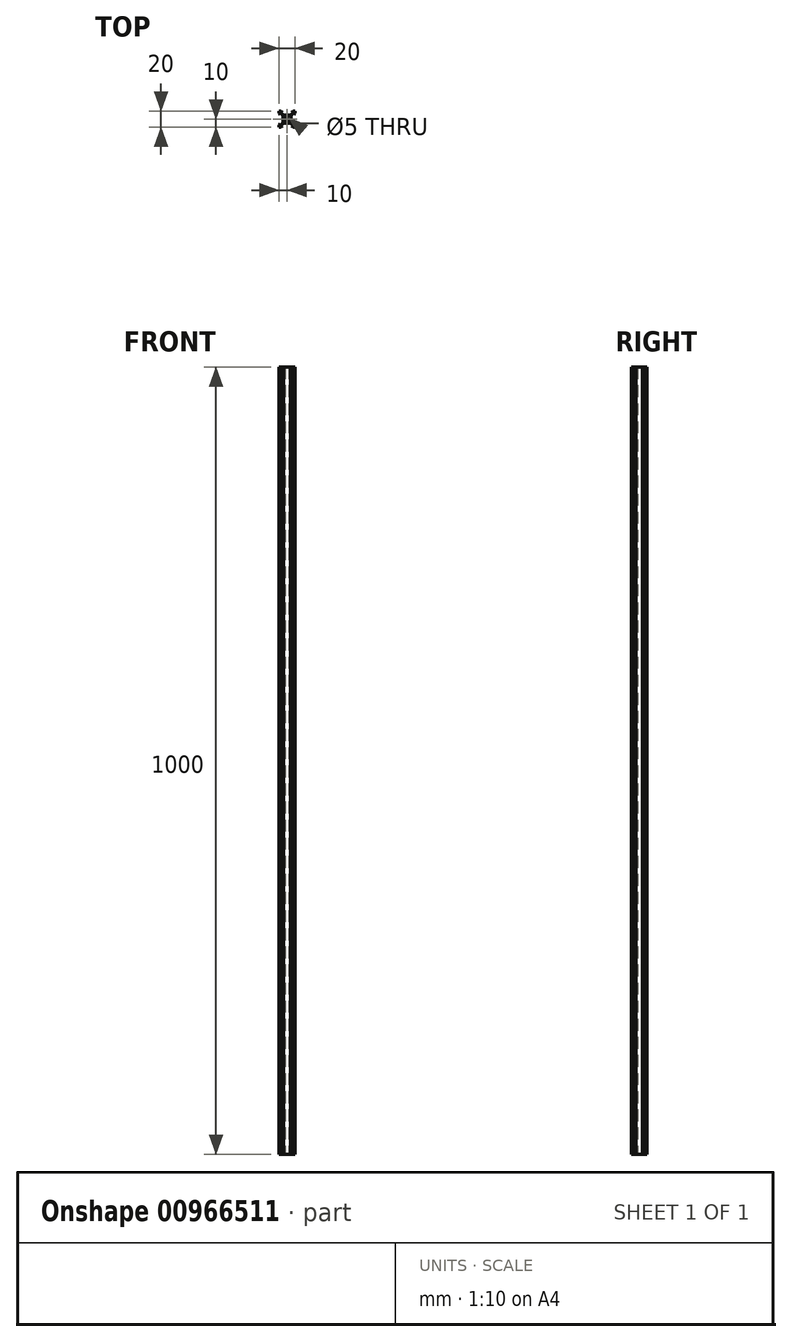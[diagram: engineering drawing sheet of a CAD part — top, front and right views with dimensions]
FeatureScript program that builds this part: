
annotation { "Feature Type Name" : "Feature", "Feature Type Description" : "" }
export const myFeature = defineFeature(function(context is Context, id is Id, definition is map)
    precondition{}
    {
        {
            var Q0;
            Q0=qCreatedBy(makeId("Top.planeOp"),FACE);
            var sketch = newSketch(context, id + "F0", { "sketchPlane" : qUnion([Q0])});
            skCircle(sketch, "E0", {"center": v(0, 0) * mm, "radius": 2.5 * mm});
            skLineSegment(sketch, "E1.bottom", {"start": v(4.25, 5) * mm, "end": v(-4.25, 5) * mm});
            skLineSegment(sketch, "E1.top", {"start": v(4.25, -5) * mm, "end": v(-4.25, -5) * mm});
            skLineSegment(sketch, "E1.left", {"start": v(5, 4.25) * mm, "end": v(5, -4.25) * mm});
            skLineSegment(sketch, "E1.right", {"start": v(-5, 4.25) * mm, "end": v(-5, -4.25) * mm});
            skLineSegment(sketch, "E2.bottom", {"start": v(10, 10) * mm, "end": v(7.5, 10) * mm});
            skLineSegment(sketch, "E2.top", {"start": v(10, -10) * mm, "end": v(7.5, -10) * mm});
            skLineSegment(sketch, "E2.left", {"start": v(10, 10) * mm, "end": v(10, 7.5) * mm});
            skLineSegment(sketch, "E2.right", {"start": v(-10, 10) * mm, "end": v(-10, 7.52) * mm});
            skLineSegment(sketch, "E3.bottom", {"start": v(7.5, 9) * mm, "end": v(5.88, 9) * mm});
            skLineSegment(sketch, "E3.top", {"start": v(7.5, -9) * mm, "end": v(5.87, -9) * mm});
            skLineSegment(sketch, "E3.left", {"start": v(7.5, 9) * mm, "end": v(7.5, 8.25) * mm});
            skLineSegment(sketch, "E3.right", {"start": v(-7.5, 9) * mm, "end": v(-7.5, 8.25) * mm});
            skLineSegment(sketch, "E4.bottom", {"start": v(9, 7.5) * mm, "end": v(8.25, 7.5) * mm});
            skLineSegment(sketch, "E4.top", {"start": v(9, -7.5) * mm, "end": v(8.25, -7.5) * mm});
            skLineSegment(sketch, "E4.left", {"start": v(9, 7.5) * mm, "end": v(9, 5.94) * mm});
            skLineSegment(sketch, "E4.right", {"start": v(-9, 7.5) * mm, "end": v(-9, 5.74) * mm});
            skLineSegment(sketch, "E5.trimOffspring", {"start": v(-8.25, 7.5) * mm, "end": v(-9, 7.5) * mm});
            skLineSegment(sketch, "E6.trimOffspring", {"start": v(-7.5, -8.25) * mm, "end": v(-7.5, -9) * mm});
            skLineSegment(sketch, "E7.trimOffspring", {"start": v(7.5, -8.25) * mm, "end": v(7.5, -9) * mm});
            skLineSegment(sketch, "E8.trimOffspring", {"start": v(-8.25, -7.5) * mm, "end": v(-9, -7.5) * mm});
            skLineSegment(sketch, "E9", {"start": v(-7.5, 8.25) * mm, "end": v(-4.25, 5) * mm});
            skLineSegment(sketch, "E10", {"start": v(-8.25, 7.5) * mm, "end": v(-5, 4.25) * mm});
            skLineSegment(sketch, "E11", {"start": v(8.25, -7.5) * mm, "end": v(5, -4.25) * mm});
            skLineSegment(sketch, "E12", {"start": v(7.5, -8.25) * mm, "end": v(4.25, -5) * mm});
            skLineSegment(sketch, "E13", {"start": v(-8.25, -7.5) * mm, "end": v(-5, -4.25) * mm});
            skLineSegment(sketch, "E14", {"start": v(-7.5, -8.25) * mm, "end": v(-4.25, -5) * mm});
            skLineSegment(sketch, "E15", {"start": v(7.5, 8.25) * mm, "end": v(4.25, 5) * mm});
            skLineSegment(sketch, "E16", {"start": v(8.25, 7.5) * mm, "end": v(5, 4.25) * mm});
            skPoint(sketch, "E17.orphan", {"position": v(-7.5, 7.5) * mm});
            skPoint(sketch, "E18.orphan", {"position": v(7.5, 7.5) * mm});
            skPoint(sketch, "E19.orphan", {"position": v(-7.5, -7.5) * mm});
            skPoint(sketch, "E20.orphan", {"position": v(7.5, -7.5) * mm});
            skPoint(sketch, "E21.orphan", {"position": v(-5, -5) * mm});
            skPoint(sketch, "E22.orphan", {"position": v(5, -5) * mm});
            skPoint(sketch, "E23.orphan", {"position": v(5, 5) * mm});
            skPoint(sketch, "E24.orphan", {"position": v(-5, 5) * mm});
            skLineSegment(sketch, "E25", {"start": v(-7.5, 10) * mm, "end": v(-5.62, 9) * mm});
            skLineSegment(sketch, "E26", {"start": v(7.5, 10) * mm, "end": v(5.88, 9) * mm});
            skPoint(sketch, "E26.endSnap0", {"position": v(5.88, 6.63) * mm});
            skLineSegment(sketch, "E27", {"start": v(10, 7.5) * mm, "end": v(9, 5.94) * mm});
            skLineSegment(sketch, "E28", {"start": v(10, -7.5) * mm, "end": v(9, -5.87) * mm});
            skPoint(sketch, "E28.endSnap0", {"position": v(6.62, -5.87) * mm});
            skLineSegment(sketch, "E29", {"start": v(7.5, -10) * mm, "end": v(5.87, -9) * mm});
            skPoint(sketch, "E29.endSnap0", {"position": v(5.87, -6.62) * mm});
            skLineSegment(sketch, "E30", {"start": v(-7.5, -10) * mm, "end": v(-5.45, -9) * mm});
            skLineSegment(sketch, "E31", {"start": v(-10, -7.5) * mm, "end": v(-9, -5.54) * mm});
            skLineSegment(sketch, "E32", {"start": v(-10, 7.52) * mm, "end": v(-9, 5.74) * mm});
            skLineSegment(sketch, "E33.trimOffspring", {"start": v(-10, -7.5) * mm, "end": v(-10, -10) * mm});
            skLineSegment(sketch, "E34.trimOffspring", {"start": v(-7.5, 10) * mm, "end": v(-10, 10) * mm});
            skLineSegment(sketch, "E35.trimOffspring", {"start": v(10, -7.5) * mm, "end": v(10, -10) * mm});
            skLineSegment(sketch, "E36.trimOffspring", {"start": v(-7.5, -10) * mm, "end": v(-10, -10) * mm});
            skLineSegment(sketch, "E37.trimOffspring", {"start": v(-5.62, 9) * mm, "end": v(-7.5, 9) * mm});
            skLineSegment(sketch, "E38.trimOffspring", {"start": v(9, -5.87) * mm, "end": v(9, -7.5) * mm});
            skLineSegment(sketch, "E39.trimOffspring", {"start": v(-5.45, -9) * mm, "end": v(-7.5, -9) * mm});
            skLineSegment(sketch, "E40.trimOffspring", {"start": v(-9, -5.54) * mm, "end": v(-9, -7.5) * mm});
            skSolve(sketch);
        }
        {
            var Q0;
            Q0=makeQuery(id+"F0.imprint","IMPRINT",FACE,{"disambiguationData":[TD([[makeQuery(id+"F0.imprint","IMPRINT",EDGE,{"derivedFrom":sQuery(id+"F0.wireOp",EDGE,"E0")}),-1.0]])]});
            extrude(context, id + "F1", {"entities" : qUnion([Q0]), "depth" : 1000 * mm, "offsetDistance" : 25 * mm});
        }
    });
